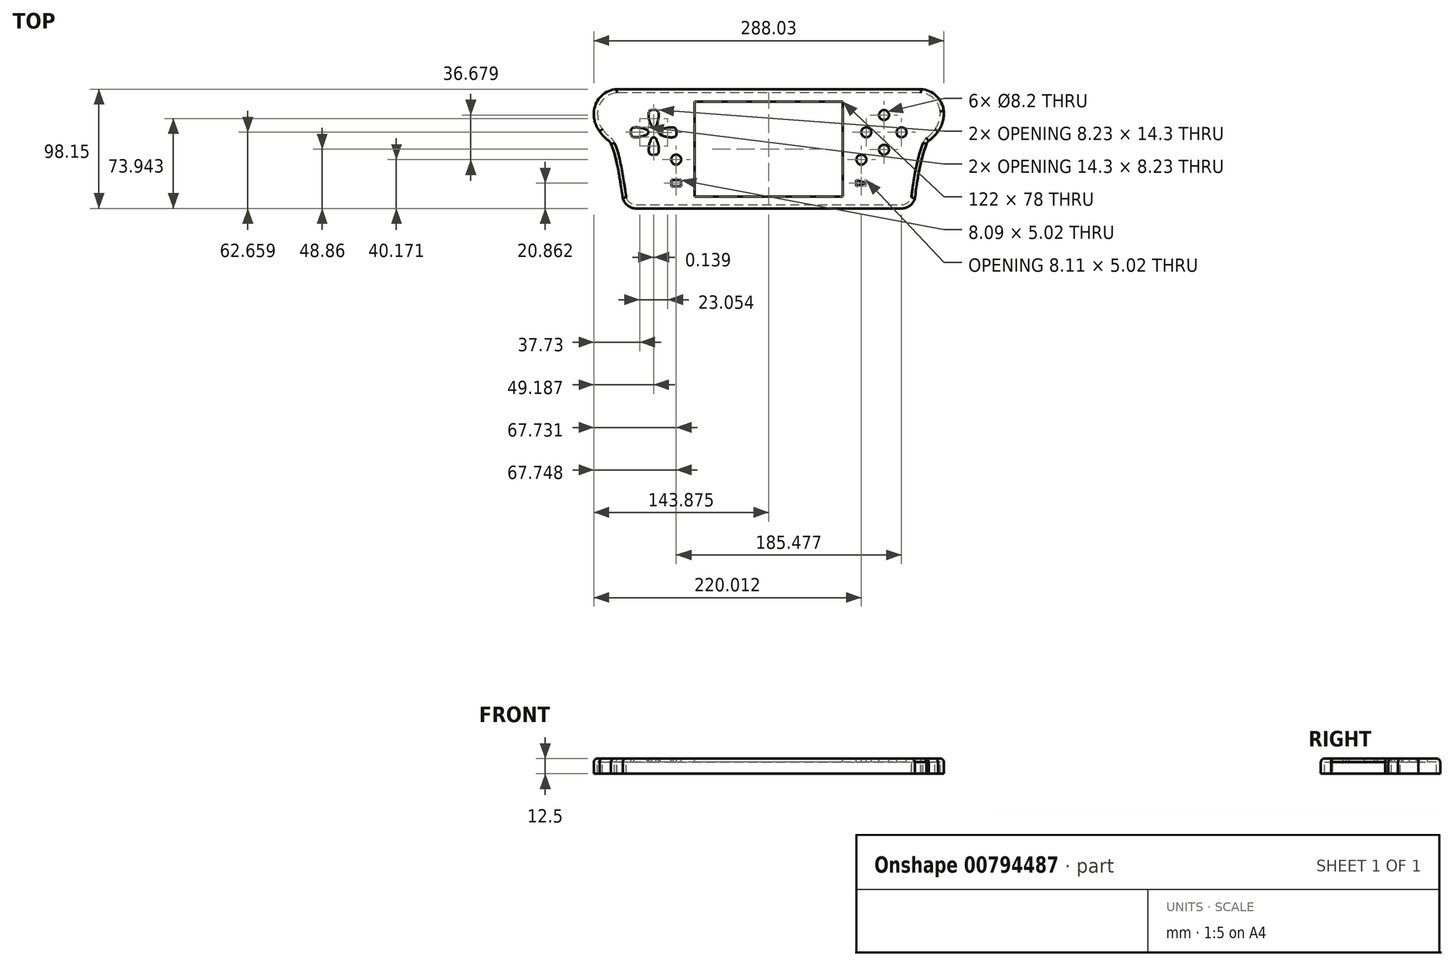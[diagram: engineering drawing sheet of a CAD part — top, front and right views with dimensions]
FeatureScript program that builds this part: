
annotation { "Feature Type Name" : "Feature", "Feature Type Description" : "" }
export const myFeature = defineFeature(function(context is Context, id is Id, definition is map)
    precondition{}
    {
        {
            var Q0;
            Q0=qCreatedBy(makeId("Top.planeOp"),FACE);
            var sketch = newSketch(context, id + "F0", { "sketchPlane" : qUnion([Q0])});
            skArc(sketch, "E0", {"start": v(0, -15.64) * mm, "mid": v(-5.18, -5.18) * mm, "end": v(-15.86, -0.46) * mm});
            skLineSegment(sketch, "E1", {"start": v(-15.86, -0.46) * mm, "end": v(-265.98, -0.46) * mm});
            skArc(sketch, "E2", {"start": v(-265.98, -0.46) * mm, "mid": v(-276.64, -5.18) * mm, "end": v(-281.8, -15.64) * mm});
            skArc(sketch, "E3", {"start": v(-4.2, -30.43) * mm, "mid": v(-0.72, -23.42) * mm, "end": v(0, -15.64) * mm});
            skArc(sketch, "E4", {"start": v(-281.8, -15.64) * mm, "mid": v(-281.24, -23.41) * mm, "end": v(-277.85, -30.43) * mm});
            skArc(sketch, "E5", {"start": v(-11.25, -37.64) * mm, "mid": v(-7.4, -34.35) * mm, "end": v(-4.2, -30.43) * mm});
            skArc(sketch, "E6", {"start": v(-277.85, -30.43) * mm, "mid": v(-274.63, -34.3) * mm, "end": v(-270.85, -37.64) * mm});
            skArc(sketch, "E7", {"start": v(-11.25, -37.64) * mm, "mid": v(-12.95, -39.42) * mm, "end": v(-13.99, -41.65) * mm});
            skArc(sketch, "E8", {"start": v(-268.03, -41.65) * mm, "mid": v(-269.13, -39.42) * mm, "end": v(-270.85, -37.64) * mm});
            skFitSpline(sketch, "E9", {"points": [v(-13.99, -41.65) * mm, v(-16.24, -47.92) * mm, v(-20.75, -66.95) * mm, v(-23.68, -86.36) * mm, v(-23.68, -86.35) * mm], "startDerivative": vector(-9.7, -25.15) * mm, "endDerivative": vector(0.08, 1.8) * mm});
            skFitSpline(sketch, "E10", {"points": [v(-268.03, -41.65) * mm, v(-265.62, -47.92) * mm, v(-261.27, -66.95) * mm, v(-258.32, -86.35) * mm], "startDerivative": vector(10.36, -23.38) * mm, "endDerivative": vector(6.58, -48.47) * mm});
            skLineSegment(sketch, "E11", {"start": v(-249.93, -92.6) * mm, "end": v(-31.97, -92.6) * mm});
            skArc(sketch, "E12", {"start": v(-31.97, -92.6) * mm, "mid": v(-26.78, -90.87) * mm, "end": v(-23.68, -86.35) * mm});
            skArc(sketch, "E13", {"start": v(-258.32, -86.35) * mm, "mid": v(-255.16, -90.87) * mm, "end": v(-249.93, -92.6) * mm});
            skSolve(sketch);
        }
        {
            var Q0;
            Q0=makeQuery(id+"F0.imprint","IMPRINT",FACE,{"disambiguationData":[TD([[makeQuery(id+"F0.imprint","IMPRINT",EDGE,{"derivedFrom":sQuery(id+"F0.wireOp",EDGE,"E0")}),1.0]])]});
            extrude(context, id + "F1", {"entities" : qUnion([Q0]), "oppositeDirection" : true, "depth" : 9.5 * mm, "offsetDistance" : 25 * mm});
        }
        {
            var Q0;
            Q0=makeQuery(id+"F1.opExtrude","CAP_FACE",FACE,{"disambiguationData":[OSD([sQuery(id+"F0.wireOp",EDGE,"E0"),sQuery(id+"F0.wireOp",EDGE,"E1"),sQuery(id+"F0.wireOp",EDGE,"E2"),sQuery(id+"F0.wireOp",EDGE,"E3"),sQuery(id+"F0.wireOp",EDGE,"E4"),sQuery(id+"F0.wireOp",EDGE,"E5"),sQuery(id+"F0.wireOp",EDGE,"E6"),sQuery(id+"F0.wireOp",EDGE,"E7"),sQuery(id+"F0.wireOp",EDGE,"E8"),sQuery(id+"F0.wireOp",EDGE,"E9"),sQuery(id+"F0.wireOp",EDGE,"E10"),sQuery(id+"F0.wireOp",EDGE,"E11"),sQuery(id+"F0.wireOp",EDGE,"E12"),sQuery(id+"F0.wireOp",EDGE,"E13")])],"isStart":false});
            shell(context, id + "F2", {"entities" : qUnion([Q0]), "thickness" : 3 * mm, "oppositeDirection" : true});
        }
        {
            var Q0;
            Q0=makeQuery(id+"F1.opExtrude","CAP_FACE",FACE,{"disambiguationData":[OSD([sQuery(id+"F0.wireOp",EDGE,"E0"),sQuery(id+"F0.wireOp",EDGE,"E1"),sQuery(id+"F0.wireOp",EDGE,"E2"),sQuery(id+"F0.wireOp",EDGE,"E3"),sQuery(id+"F0.wireOp",EDGE,"E4"),sQuery(id+"F0.wireOp",EDGE,"E5"),sQuery(id+"F0.wireOp",EDGE,"E6"),sQuery(id+"F0.wireOp",EDGE,"E7"),sQuery(id+"F0.wireOp",EDGE,"E8"),sQuery(id+"F0.wireOp",EDGE,"E9"),sQuery(id+"F0.wireOp",EDGE,"E10"),sQuery(id+"F0.wireOp",EDGE,"E11"),sQuery(id+"F0.wireOp",EDGE,"E12"),sQuery(id+"F0.wireOp",EDGE,"E13")])],"isStart":true});
            fillet(context, id + "F3", {"entities" : qUnion([Q0]), "radius" : 3 * mm, "tangentPropagation" : true, "allowEdgeOverflow" : false});
        }
        {
            var Q0;
            Q0=makeQuery(id+"F1.opExtrude","CAP_FACE",FACE,{"disambiguationData":[OSD([sQuery(id+"F0.wireOp",EDGE,"E0"),sQuery(id+"F0.wireOp",EDGE,"E1"),sQuery(id+"F0.wireOp",EDGE,"E2"),sQuery(id+"F0.wireOp",EDGE,"E3"),sQuery(id+"F0.wireOp",EDGE,"E4"),sQuery(id+"F0.wireOp",EDGE,"E5"),sQuery(id+"F0.wireOp",EDGE,"E6"),sQuery(id+"F0.wireOp",EDGE,"E7"),sQuery(id+"F0.wireOp",EDGE,"E8"),sQuery(id+"F0.wireOp",EDGE,"E9"),sQuery(id+"F0.wireOp",EDGE,"E10"),sQuery(id+"F0.wireOp",EDGE,"E11"),sQuery(id+"F0.wireOp",EDGE,"E12"),sQuery(id+"F0.wireOp",EDGE,"E13")])],"isStart":true});
            var sketch = newSketch(context, id + "F4", { "sketchPlane" : qUnion([Q0])});
            skCircle(sketch, "E14", {"center": v(-217.2, -55.42) * mm, "radius": 4.1 * mm});
            skCircle(sketch, "E15", {"center": v(-64.8, -55.44) * mm, "radius": 4.1 * mm});
            skCircle(sketch, "E16", {"center": v(-60.73, -32.94) * mm, "radius": 4.1 * mm});
            skCircle(sketch, "E17", {"center": v(-31.73, -32.94) * mm, "radius": 4.1 * mm});
            skCircle(sketch, "E18", {"center": v(-46.18, -18.76) * mm, "radius": 4.1 * mm});
            skCircle(sketch, "E19", {"center": v(-46.18, -47.25) * mm, "radius": 4.1 * mm});
            skLineSegment(sketch, "E20", {"start": v(-68.98, -72.24) * mm, "end": v(-68.98, -77.26) * mm});
            skLineSegment(sketch, "E21", {"start": v(-68.98, -77.26) * mm, "end": v(-60.87, -74.79) * mm});
            skLineSegment(sketch, "E22", {"start": v(-60.87, -74.79) * mm, "end": v(-68.98, -72.24) * mm});
            skLineSegment(sketch, "E23", {"start": v(-221.23, -72.24) * mm, "end": v(-221.23, -77.26) * mm});
            skLineSegment(sketch, "E24", {"start": v(-221.23, -77.26) * mm, "end": v(-213.15, -77.26) * mm});
            skLineSegment(sketch, "E25", {"start": v(-213.15, -77.26) * mm, "end": v(-213.15, -72.24) * mm});
            skLineSegment(sketch, "E26", {"start": v(-213.15, -72.24) * mm, "end": v(-221.23, -72.24) * mm});
            skArc(sketch, "E27", {"start": v(-237.23, -14.57) * mm, "mid": v(-239, -15.29) * mm, "end": v(-239.82, -17.01) * mm});
            skLineSegment(sketch, "E28", {"start": v(-237.23, -14.57) * mm, "end": v(-234.38, -14.52) * mm});
            skArc(sketch, "E29", {"start": v(-231.72, -17.01) * mm, "mid": v(-232.54, -15.22) * mm, "end": v(-234.38, -14.52) * mm});
            skArc(sketch, "E30", {"start": v(-233.86, -27.8) * mm, "mid": v(-232, -22.56) * mm, "end": v(-231.72, -17.01) * mm});
            skArc(sketch, "E31", {"start": v(-239.82, -17.01) * mm, "mid": v(-239.41, -22.57) * mm, "end": v(-237.45, -27.8) * mm});
            skArc(sketch, "E32", {"start": v(-237.45, -27.8) * mm, "mid": v(-235.65, -28.82) * mm, "end": v(-233.86, -27.8) * mm});
            skArc(sketch, "E33", {"start": v(-254.31, -34.42) * mm, "mid": v(-253.6, -36.2) * mm, "end": v(-251.87, -37.02) * mm});
            skLineSegment(sketch, "E34", {"start": v(-254.31, -34.42) * mm, "end": v(-254.36, -31.58) * mm});
            skArc(sketch, "E35", {"start": v(-251.87, -28.92) * mm, "mid": v(-253.65, -29.74) * mm, "end": v(-254.36, -31.58) * mm});
            skArc(sketch, "E36", {"start": v(-241.09, -31.06) * mm, "mid": v(-246.32, -29.2) * mm, "end": v(-251.87, -28.92) * mm});
            skArc(sketch, "E37", {"start": v(-251.87, -37.02) * mm, "mid": v(-246.3, -36.61) * mm, "end": v(-241.09, -34.64) * mm});
            skArc(sketch, "E38", {"start": v(-241.09, -34.64) * mm, "mid": v(-240.06, -32.85) * mm, "end": v(-241.09, -31.06) * mm});
            skArc(sketch, "E39", {"start": v(-234.14, -51.38) * mm, "mid": v(-232.37, -50.66) * mm, "end": v(-231.54, -48.93) * mm});
            skLineSegment(sketch, "E40", {"start": v(-234.14, -51.38) * mm, "end": v(-236.99, -51.43) * mm});
            skArc(sketch, "E41", {"start": v(-239.65, -48.93) * mm, "mid": v(-238.82, -50.72) * mm, "end": v(-236.99, -51.43) * mm});
            skArc(sketch, "E42", {"start": v(-237.5, -38.15) * mm, "mid": v(-239.37, -43.39) * mm, "end": v(-239.65, -48.93) * mm});
            skArc(sketch, "E43", {"start": v(-231.54, -48.93) * mm, "mid": v(-231.95, -43.37) * mm, "end": v(-233.92, -38.15) * mm});
            skArc(sketch, "E44", {"start": v(-233.92, -38.15) * mm, "mid": v(-235.71, -37.13) * mm, "end": v(-237.5, -38.15) * mm});
            skArc(sketch, "E45", {"start": v(-217.06, -31.52) * mm, "mid": v(-217.78, -29.75) * mm, "end": v(-219.5, -28.92) * mm});
            skLineSegment(sketch, "E46", {"start": v(-217.06, -31.52) * mm, "end": v(-217, -34.36) * mm});
            skArc(sketch, "E47", {"start": v(-219.5, -37.03) * mm, "mid": v(-217.71, -36.2) * mm, "end": v(-217, -34.36) * mm});
            skArc(sketch, "E48", {"start": v(-230.28, -34.88) * mm, "mid": v(-225.05, -36.75) * mm, "end": v(-219.5, -37.03) * mm});
            skArc(sketch, "E49", {"start": v(-219.5, -28.92) * mm, "mid": v(-225.06, -29.33) * mm, "end": v(-230.28, -31.3) * mm});
            skArc(sketch, "E50", {"start": v(-230.28, -31.3) * mm, "mid": v(-231.3, -33.1) * mm, "end": v(-230.28, -34.88) * mm});
            skSolve(sketch);
        }
        {
            var Q0;
            Q0=makeQuery(id+"F4.imprint","IMPRINT",FACE,{"disambiguationData":[TD([[makeQuery(id+"F4.imprint","IMPRINT",EDGE,{"derivedFrom":sQuery(id+"F4.wireOp",EDGE,"E27")}),1.0]])]});
            var Q1;
            Q1=makeQuery(id+"F4.imprint","IMPRINT",FACE,{"disambiguationData":[TD([[makeQuery(id+"F4.imprint","IMPRINT",EDGE,{"derivedFrom":sQuery(id+"F4.wireOp",EDGE,"E33")}),1.0]])]});
            var Q2;
            Q2=makeQuery(id+"F4.imprint","IMPRINT",FACE,{"disambiguationData":[TD([[makeQuery(id+"F4.imprint","IMPRINT",EDGE,{"derivedFrom":sQuery(id+"F4.wireOp",EDGE,"E45")}),1.0]])]});
            var Q3;
            Q3=makeQuery(id+"F4.imprint","IMPRINT",FACE,{"disambiguationData":[TD([[makeQuery(id+"F4.imprint","IMPRINT",EDGE,{"derivedFrom":sQuery(id+"F4.wireOp",EDGE,"E39")}),1.0]])]});
            var Q4;
            Q4=makeQuery(id+"F4.imprint","IMPRINT",FACE,{"disambiguationData":[TD([[makeQuery(id+"F4.imprint","IMPRINT",EDGE,{"derivedFrom":sQuery(id+"F4.wireOp",EDGE,"E14")}),1.0]])]});
            var Q5;
            Q5=makeQuery(id+"F4.imprint","IMPRINT",FACE,{"disambiguationData":[TD([[makeQuery(id+"F4.imprint","IMPRINT",EDGE,{"derivedFrom":sQuery(id+"F4.wireOp",EDGE,"E23")}),1.0]])]});
            var Q6;
            Q6=makeQuery(id+"F4.imprint","IMPRINT",FACE,{"disambiguationData":[TD([[makeQuery(id+"F4.imprint","IMPRINT",EDGE,{"derivedFrom":sQuery(id+"F4.wireOp",EDGE,"E20")}),1.0]])]});
            var Q7;
            Q7=makeQuery(id+"F4.imprint","IMPRINT",FACE,{"disambiguationData":[TD([[makeQuery(id+"F4.imprint","IMPRINT",EDGE,{"derivedFrom":sQuery(id+"F4.wireOp",EDGE,"E15")}),1.0]])]});
            var Q8;
            Q8=makeQuery(id+"F4.imprint","IMPRINT",FACE,{"disambiguationData":[TD([[makeQuery(id+"F4.imprint","IMPRINT",EDGE,{"derivedFrom":sQuery(id+"F4.wireOp",EDGE,"E16")}),1.0]])]});
            var Q9;
            Q9=makeQuery(id+"F4.imprint","IMPRINT",FACE,{"disambiguationData":[TD([[makeQuery(id+"F4.imprint","IMPRINT",EDGE,{"derivedFrom":sQuery(id+"F4.wireOp",EDGE,"E18")}),1.0]])]});
            var Q10;
            Q10=makeQuery(id+"F4.imprint","IMPRINT",FACE,{"disambiguationData":[TD([[makeQuery(id+"F4.imprint","IMPRINT",EDGE,{"derivedFrom":sQuery(id+"F4.wireOp",EDGE,"E17")}),1.0]])]});
            var Q11;
            Q11=makeQuery(id+"F4.imprint","IMPRINT",FACE,{"disambiguationData":[TD([[makeQuery(id+"F4.imprint","IMPRINT",EDGE,{"derivedFrom":sQuery(id+"F4.wireOp",EDGE,"E19")}),1.0]])]});
            extrude(context, id + "F5", {"entities" : qUnion([Q0, Q1, Q2, Q3, Q4, Q5, Q6, Q7, Q8, Q9, Q10, Q11]), "operationType" : NewBodyOperationType.REMOVE, "endBound" : BoundingType.SYMMETRIC, "oppositeDirection" : true, "depth" : 10 * mm, "offsetDistance" : 25 * mm});
        }
        {
            var Q0;
            Q0=makeQuery(id+"F1.opExtrude","CAP_FACE",FACE,{"disambiguationData":[OSD([sQuery(id+"F0.wireOp",EDGE,"E0"),sQuery(id+"F0.wireOp",EDGE,"E1"),sQuery(id+"F0.wireOp",EDGE,"E2"),sQuery(id+"F0.wireOp",EDGE,"E3"),sQuery(id+"F0.wireOp",EDGE,"E4"),sQuery(id+"F0.wireOp",EDGE,"E5"),sQuery(id+"F0.wireOp",EDGE,"E6"),sQuery(id+"F0.wireOp",EDGE,"E7"),sQuery(id+"F0.wireOp",EDGE,"E8"),sQuery(id+"F0.wireOp",EDGE,"E9"),sQuery(id+"F0.wireOp",EDGE,"E10"),sQuery(id+"F0.wireOp",EDGE,"E11"),sQuery(id+"F0.wireOp",EDGE,"E12"),sQuery(id+"F0.wireOp",EDGE,"E13")])],"isStart":true});
            var sketch = newSketch(context, id + "F6", { "sketchPlane" : qUnion([Q0])});
            skLineSegment(sketch, "E51.bottom", {"start": v(-202.06, -7.75) * mm, "end": v(-80.06, -7.75) * mm});
            skLineSegment(sketch, "E51.top", {"start": v(-202.06, -85.75) * mm, "end": v(-80.06, -85.75) * mm});
            skLineSegment(sketch, "E51.left", {"start": v(-202.06, -7.75) * mm, "end": v(-202.06, -85.75) * mm});
            skLineSegment(sketch, "E51.right", {"start": v(-80.06, -7.75) * mm, "end": v(-80.06, -85.75) * mm});
            skSolve(sketch);
        }
        {
            var Q0;
            Q0=makeQuery(id+"F6.imprint","IMPRINT",FACE,{"disambiguationData":[TD([[makeQuery(id+"F6.imprint","IMPRINT",EDGE,{"derivedFrom":sQuery(id+"F6.wireOp",EDGE,"E51.bottom")}),-1.0]])]});
            extrude(context, id + "F7", {"entities" : qUnion([Q0]), "operationType" : NewBodyOperationType.REMOVE, "endBound" : BoundingType.UP_TO_NEXT, "oppositeDirection" : true, "depth" : 25 * mm, "offsetDistance" : 25 * mm});
        }
    });
